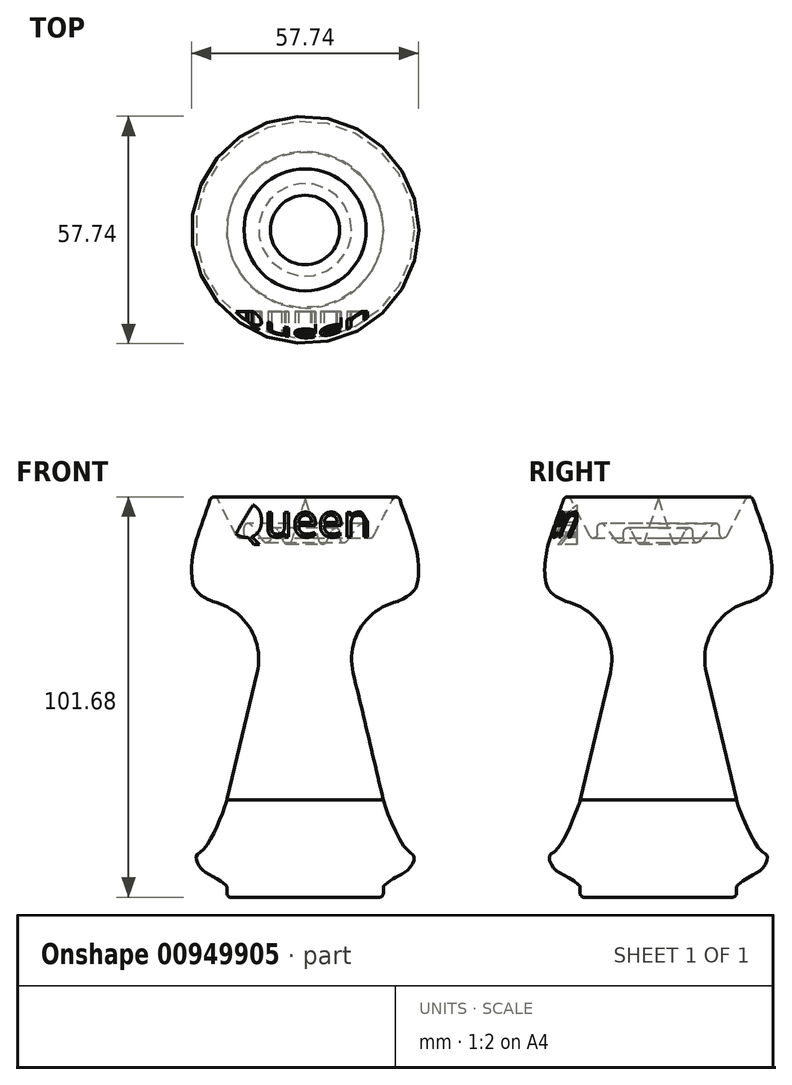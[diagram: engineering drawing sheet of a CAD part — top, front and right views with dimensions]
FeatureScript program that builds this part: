
annotation { "Feature Type Name" : "Feature", "Feature Type Description" : "" }
export const myFeature = defineFeature(function(context is Context, id is Id, definition is map)
    precondition{}
    {
        {
            var Q0;
            Q0=qCreatedBy(makeId("Front.planeOp"),FACE);
            var sketch = newSketch(context, id + "F0", { "sketchPlane" : qUnion([Q0])});
            skLineSegment(sketch, "E0", {"start": v(0, 46) * mm, "end": v(0, -55.25) * mm});
            skLineSegment(sketch, "E1", {"start": v(0, -55.25) * mm, "end": v(19.87, -55.25) * mm});
            skLineSegment(sketch, "E2", {"start": v(19.87, -55.25) * mm, "end": v(19.87, -52.35) * mm});
            skFitSpline(sketch, "E3", {"points": [v(19.87, -52.35) * mm, v(21.86, -50.9) * mm, v(24.04, -49.63) * mm, v(26.58, -47.81) * mm, v(27.67, -44.9) * mm, v(25.31, -42.55) * mm, v(19.87, -30.57) * mm, v(19.87, -30.4) * mm], "startDerivative": vector(15.77, 12.02) * mm, "endDerivative": vector(1.1, 2.52) * mm});
            skLineSegment(sketch, "E4", {"start": v(19.87, -30.4) * mm, "end": v(7.9, 19.87) * mm});
            skLineSegment(sketch, "E5", {"start": v(7.9, 19.87) * mm, "end": v(23.5, 19.87) * mm});
            skFitSpline(sketch, "E6", {"points": [v(23.5, 19.87) * mm, v(27.49, 22.4) * mm, v(28.76, 25.86) * mm, v(28.58, 31.48) * mm, v(26.95, 37.65) * mm, v(24.95, 43.28) * mm, v(23.5, 47.81) * mm, v(23.5, 48.18) * mm, v(23.5, 48.36) * mm], "startDerivative": vector(31.12, 15.03) * mm, "endDerivative": vector(-0.24, 6.22) * mm});
            skLineSegment(sketch, "E7", {"start": v(23.5, 48.3) * mm, "end": v(15.51, 32.93) * mm});
            skLineSegment(sketch, "E8", {"start": v(15.51, 32.93) * mm, "end": v(15.51, 41.64) * mm});
            skLineSegment(sketch, "E9", {"start": v(15.51, 41.64) * mm, "end": v(8.8, 32.93) * mm});
            skLineSegment(sketch, "E10", {"start": v(8.8, 32.93) * mm, "end": v(8.8, 41.64) * mm});
            skLineSegment(sketch, "E11", {"start": v(8.8, 41.64) * mm, "end": v(4.27, 32.93) * mm});
            skLineSegment(sketch, "E12", {"start": v(4.27, 32.93) * mm, "end": v(0, 46) * mm});
            skSolve(sketch);
        }
        {
            var Q0;
            Q0=qSketchRegion(id+"F0",true);
            var Q1;
            Q1=sQuery(id+"F0.wireOp",EDGE,"E0");
            revolve(context, id + "F1", {"surfaceOperationType" : NewSurfaceOperationType.NEW, "entities" : qUnion([Q0]), "axis" : qUnion([Q1]), "revolveType" : RevolveType.FULL});
        }
        {
            var Q0;
            Q0=qCreatedBy(makeId("Front.planeOp"),FACE);
            cPlane(context, id + "F2", {"entities" : qUnion([Q0]), "cplaneType" : CPlaneType.OFFSET, "offset" : 38.8 * mm, "width" : 150 * mm, "height" : 150 * mm});
        }
        {
            var Q0;
            Q0=qCreatedBy(id+"F2.planeOp",FACE);
            var sketch = newSketch(context, id + "F3", { "sketchPlane" : qUnion([Q0])});
            skText(sketch, "E13", { "text": "Queen", "fontName": "OpenSans-Regular.ttf"});
            const initialGuessF3  = {"E13": [-0.01938, 0.0363, 1, 0, 0.00833]};
            skSetInitialGuess(sketch, initialGuessF3);
            skSolve(sketch);
        }
        {
            var Q0;
            Q0=qSketchRegion(id+"F3",true);
            var Q1;
            Q1=makeQuery(id+"F3.imprint","IMPRINT",FACE,{"disambiguationData":[TD([[makeQuery(id+"F3.imprint","IMPRINT",EDGE,{"derivedFrom":sQuery(id+"F3.wireOp",EDGE,"E13.sketch_text.stroke-12")}),1.0]])]});
            extrude(context, id + "F4", {"entities" : qUnion([Q0, Q1]), "operationType" : NewBodyOperationType.REMOVE, "oppositeDirection" : true, "depth" : 18.1 * mm, "offsetDistance" : 25 * mm});
        }
        {
            var Q0;
            Q0=makeQuery(id+"F1.opRevolve","SWEPT_EDGE",EDGE,{"disambiguationData":[OSD([sQuery(id+"F0.wireOp",EDGE,"E1"),sQuery(id+"F0.wireOp",EDGE,"E2")])]});
            var Q1;
            Q1=makeQuery(id+"F1.opRevolve","SWEPT_EDGE",EDGE,{"disambiguationData":[OSD([sQuery(id+"F0.wireOp",EDGE,"E2"),sQuery(id+"F0.wireOp",EDGE,"E3")])]});
            var Q2;
            Q2=makeQuery(id+"F1.opRevolve","SWEPT_EDGE",EDGE,{"disambiguationData":[OSD([sQuery(id+"F0.wireOp",EDGE,"E3"),sQuery(id+"F0.wireOp",EDGE,"E4")])]});
            var Q3;
            Q3=makeQuery(id+"F1.opRevolve","SWEPT_EDGE",EDGE,{"disambiguationData":[OSD([sQuery(id+"F0.wireOp",EDGE,"E5"),sQuery(id+"F0.wireOp",EDGE,"E6")])]});
            fillet(context, id + "F5", {"entities" : qUnion([Q0, Q1, Q2, Q3]), "radius" : 1 * mm, "tangentPropagation" : true, "allowEdgeOverflow" : false});
        }
        {
            var Q0;
            Q0=makeQuery(id+"F1.opRevolve","SWEPT_EDGE",EDGE,{"disambiguationData":[OSD([sQuery(id+"F0.wireOp",EDGE,"E4"),sQuery(id+"F0.wireOp",EDGE,"E5")])]});
            fillet(context, id + "F6", {"entities" : qUnion([Q0]), "radius" : 15 * mm, "tangentPropagation" : true, "allowEdgeOverflow" : false});
        }
        {
            var Q0;
            Q0=makeQuery(id+"F1.opRevolve","SWEPT_EDGE",EDGE,{"disambiguationData":[OSD([sQuery(id+"F0.wireOp",EDGE,"E6"),sQuery(id+"F0.wireOp",EDGE,"E7")])]});
            fillet(context, id + "F7", {"entities" : qUnion([Q0]), "radius" : 1 * mm, "tangentPropagation" : true, "allowEdgeOverflow" : false});
        }
        {
            var Q0;
            Q0=makeQuery(id+"F1.opRevolve","SWEPT_EDGE",EDGE,{"disambiguationData":[OSD([sQuery(id+"F0.wireOp",EDGE,"E8"),sQuery(id+"F0.wireOp",EDGE,"E9")])]});
            var Q1;
            Q1=makeQuery(id+"F1.opRevolve","SWEPT_EDGE",EDGE,{"disambiguationData":[OSD([sQuery(id+"F0.wireOp",EDGE,"E11"),sQuery(id+"F0.wireOp",EDGE,"E12")])]});
            var Q2;
            Q2=makeQuery(id+"F1.opRevolve","SWEPT_EDGE",EDGE,{"disambiguationData":[OSD([sQuery(id+"F0.wireOp",EDGE,"E10"),sQuery(id+"F0.wireOp",EDGE,"E11")])]});
            var Q3;
            Q3=makeQuery(id+"F1.opRevolve","SWEPT_EDGE",EDGE,{"disambiguationData":[OSD([sQuery(id+"F0.wireOp",EDGE,"E9"),sQuery(id+"F0.wireOp",EDGE,"E10")])]});
            var Q4;
            Q4=makeQuery(id+"F1.opRevolve","SWEPT_EDGE",EDGE,{"disambiguationData":[OSD([sQuery(id+"F0.wireOp",EDGE,"E7"),sQuery(id+"F0.wireOp",EDGE,"E8")])]});
            var Q5;
            Q5=makeQuery(id+"F1.opRevolve","SWEPT_FACE",FACE,{"disambiguationData":[OSD([sQuery(id+"F0.wireOp",EDGE,"E12")])]});
            fillet(context, id + "F8", {"entities" : qUnion([Q0, Q1, Q2, Q3, Q4, Q5]), "radius" : 1 * mm, "tangentPropagation" : true, "allowEdgeOverflow" : false});
        }
    });
